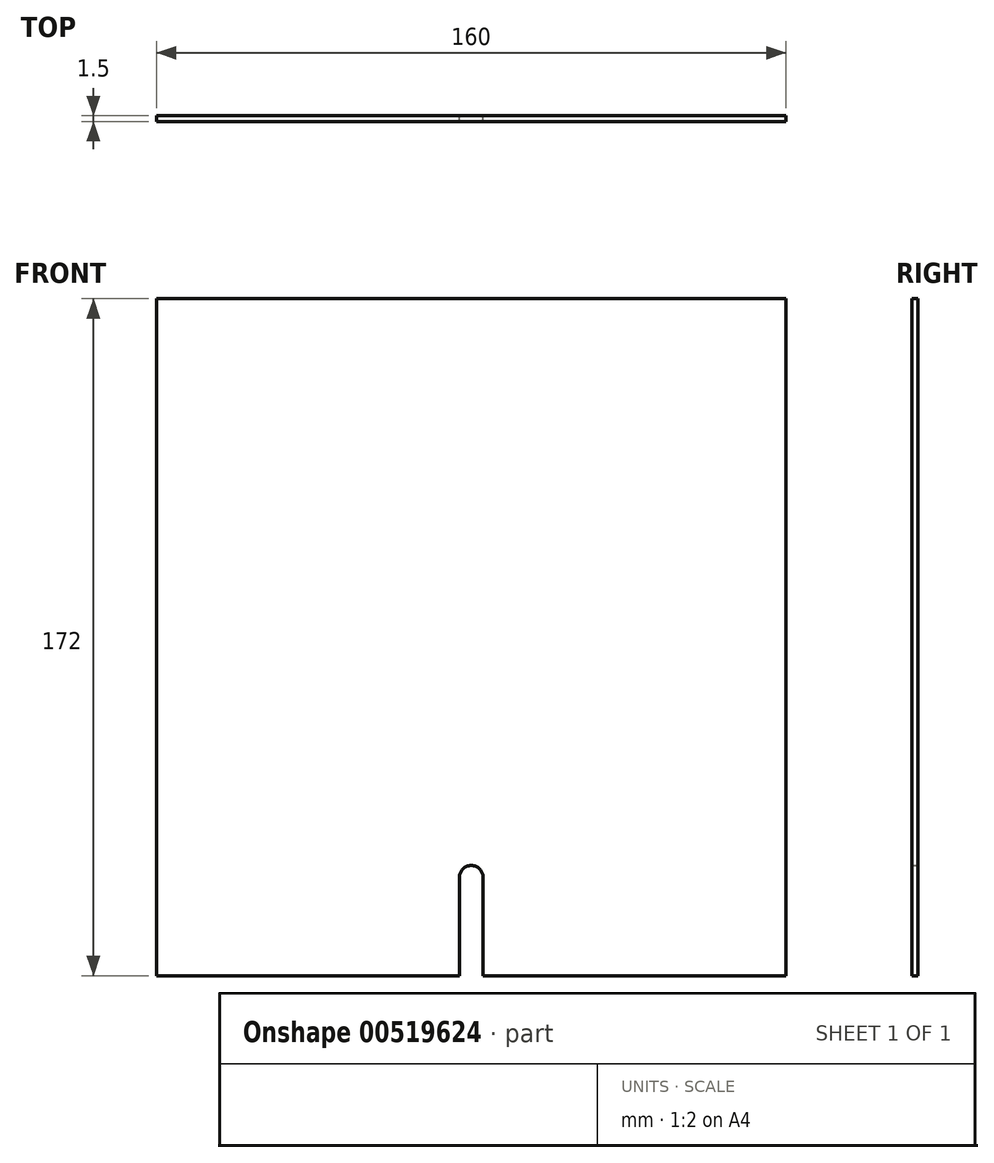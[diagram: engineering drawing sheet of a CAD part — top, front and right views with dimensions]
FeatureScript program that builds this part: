
annotation { "Feature Type Name" : "Feature", "Feature Type Description" : "" }
export const myFeature = defineFeature(function(context is Context, id is Id, definition is map)
    precondition{}
    {
        {
            var Q0;
            Q0=qCreatedBy(makeId("Front.planeOp"),FACE);
            var sketch = newSketch(context, id + "F0", { "sketchPlane" : qUnion([Q0])});
            skLineSegment(sketch, "E0.bottom", {"start": v(80, 86) * mm, "end": v(-80, 86) * mm});
            skLineSegment(sketch, "E0.top", {"start": v(80, -86) * mm, "end": v(3, -86) * mm});
            skLineSegment(sketch, "E0.left", {"start": v(80, 86) * mm, "end": v(80, -86) * mm});
            skLineSegment(sketch, "E0.right", {"start": v(-80, 86) * mm, "end": v(-80, -86) * mm});
            skPoint(sketch, "E0.middle", {"position": v(0, 0) * mm});
            skArc(sketch, "E1", {"start": v(3, -61) * mm, "mid": v(0, -58) * mm, "end": v(-3, -61) * mm});
            skPoint(sketch, "E1.centerSnap0", {"position": v(0, -86) * mm});
            skLineSegment(sketch, "E2.left", {"start": v(3, -61) * mm, "end": v(3, -86) * mm});
            skLineSegment(sketch, "E2.right", {"start": v(-3, -61) * mm, "end": v(-3, -86) * mm});
            skLineSegment(sketch, "E3.trimOffspring", {"start": v(-3, -86) * mm, "end": v(-80, -86) * mm});
            skSolve(sketch);
        }
        {
            var Q0;
            Q0=makeQuery(id+"F0.imprint","IMPRINT",FACE,{"disambiguationData":[TD([[makeQuery(id+"F0.imprint","IMPRINT",EDGE,{"derivedFrom":sQuery(id+"F0.wireOp",EDGE,"E0.bottom")}),1.0]])]});
            extrude(context, id + "F1", {"entities" : qUnion([Q0]), "depth" : 1.5 * mm, "offsetDistance" : 25 * mm});
        }
    });
